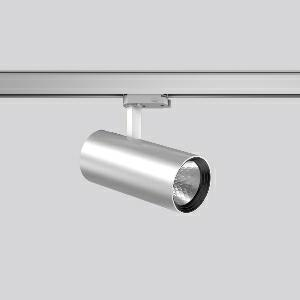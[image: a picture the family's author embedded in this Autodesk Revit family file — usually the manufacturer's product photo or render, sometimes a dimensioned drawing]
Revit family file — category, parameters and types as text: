
# Revit family: deecos_s_mini_742205_004_1_76_9464
name_source: partatom
category: Lighting Fixtures
units: mm (PartAtom-declared; Revit-internal decimal feet)

## family parameters
Cut with Voids When Loaded = No
Host = Face
Light Source = No
Part Type = Normal
Room Calculation Point = No
Round Connector Dimension = Use Diameter
Shared = No

## types (1)
- DEECOS S mini (1 x LED Modul 940, 3900 lm, 4000)
    Apparent Load = 29 VA
    Approval mark = CE
    CIE Flux Codes = 95 99 100 100 100
    Color Rendering = 92
    Color Temperature = 4000
    Default Elevation = 1800 mm
    Description = Series: DEECOS S mini
LED surface-mounted projector in modern design with no visible cooling ribs. Housing: die-cast aluminium, powder-coated. Rotation range: 356°. Swivel range: 90°. Black plastic ring and recessed LED to prevent glare from the side. Optical assembly with reflector made of MIRO-Silver with 98% total light reflection for outstanding efficiency - can be changed without tools. Best colour rendering index Ra>90. With adapter for RZB 3-circuit DALI tracks. Suitable for Track on ceiling, Wall track. High quality converter without flickering and stroboscopic effect. The following accessories can be mounted without use of tools: interchangeable lenses, decorative glasses, honeycomb louvre, clear and frosted diffusers, white interchangeable plastic ring. 
Colour: silver
Diameter: 87 mm
Height: 214 mm
Lamp: LED
Socket: without socket
Colour temperature: 4000K
Colour rendering index (CRI): 92
System power: 29 W
Rated luminous flux: 3900 lm
Luminous efficiency: 134 lm/W
Control gear: Converter, dimmable, DALI
Protection class: I
Type of protection: IP 20
    Height = 214 mm
    Lamp = 1 x LED Modul 940
    Lamp Light Flux = 3900 lm
    Lamp count = 1
    Length = 87 mm
    Lifetime = 50000 h
    Luminous efficacy = 134 lm/W
    Manufacturer = RZB
    ModVariant = No
    Model = 742205.004.1.76
    Mounting Place = Ceiling
    Mounting Type = Rail mounted
    Number of Poles = 1
    OnlyDefault = Yes
    Power Factor = 1
    Product Name = DEECOS S mini
    Product group = Track mounted projectors
    ProductGroupID = 301
    Protection Class = Protection class I
    Protection Degree = IP 20
    RLX_Detail_Level = 1
    RLX_Emergency_Light_Flux = 0 lm
    RLX_Emergency_Type = 0
    RLX_Emergency_Type_DB = No
    RlxData = <blob elided: 38057 chars, md5=82341053>
    Socket = socket
    Standby Power = 0 W
    System Light Flux = 3900 lm
    System Power = 29 W
    Type Comments = Product without accessories
    Type Image = 741926.004.jpg
    URL = http://relux.com
    VarID = ---
    Voltage = 230 V
    Voltage Range = 220-240 V
    Weight = 0.00 kg
    Width = 0 mm  [stored 0 ft]

note: [stored X ft] marks values corroborated as IEEE doubles in the binary element streams (Revit-internal decimal feet)

## geometry (parser evidence)
native form markers: Blend x4, Sweep x12
no freeform markers — native parametric forms only
